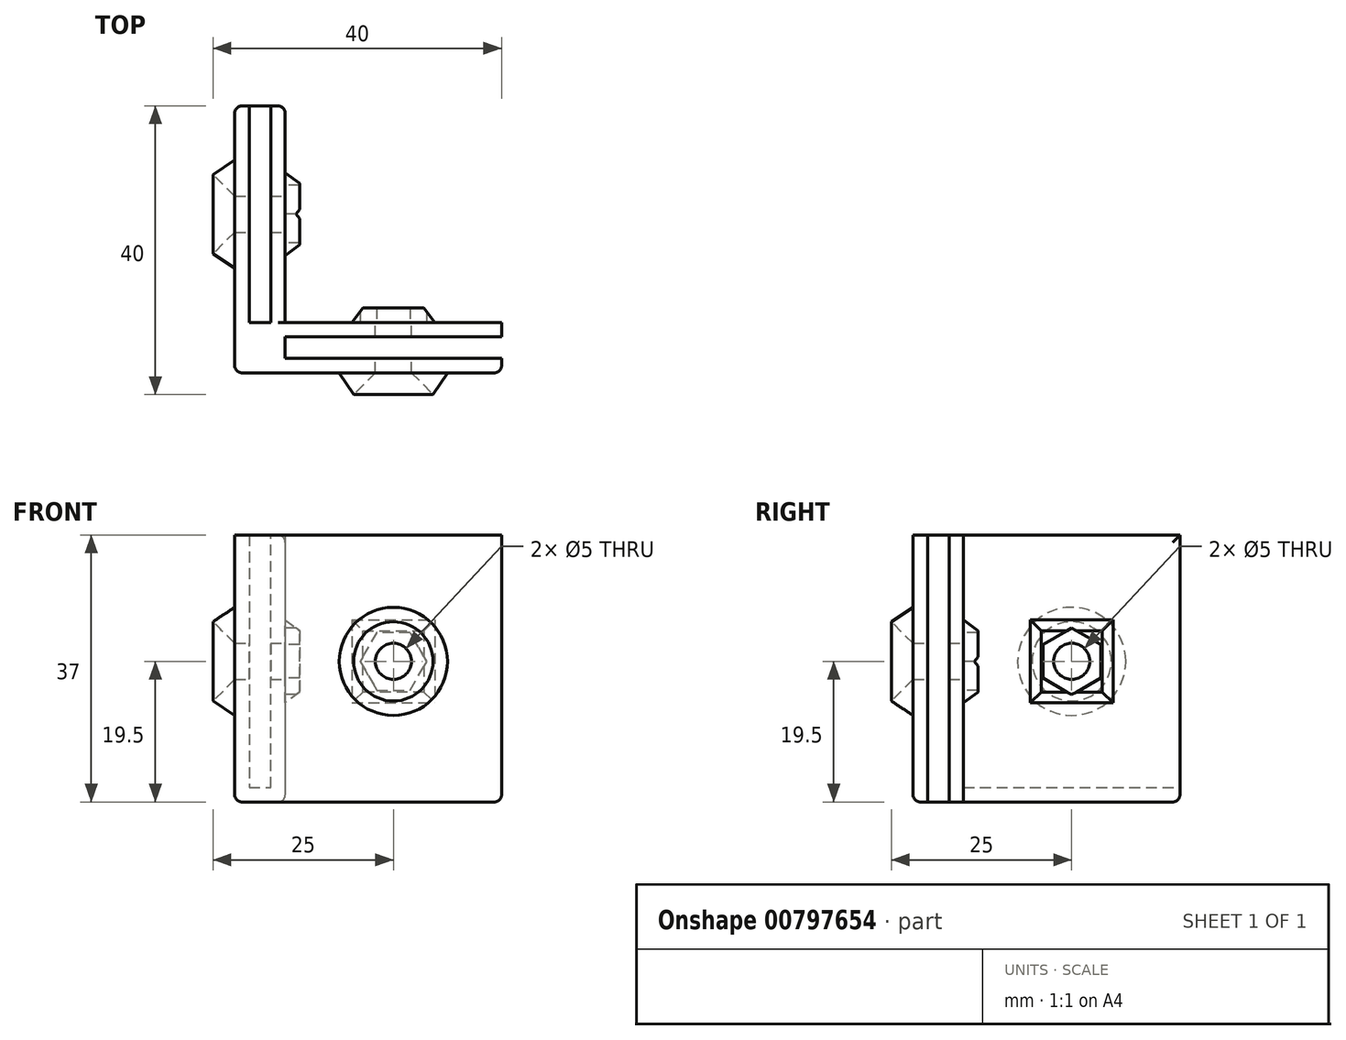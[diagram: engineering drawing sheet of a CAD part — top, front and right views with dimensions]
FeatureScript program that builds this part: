
annotation { "Feature Type Name" : "Feature", "Feature Type Description" : "" }
export const myFeature = defineFeature(function(context is Context, id is Id, definition is map)
    precondition{}
    {
        {
            var Q0;
            Q0=qCreatedBy(makeId("Front.planeOp"),FACE);
            var sketch = newSketch(context, id + "F0", { "sketchPlane" : qUnion([Q0])});
            skLineSegment(sketch, "E0.bottom", {"start": v(18.5, -18.5) * mm, "end": v(-18.5, -18.5) * mm});
            skLineSegment(sketch, "E0.top", {"start": v(18.5, 18.5) * mm, "end": v(-18.5, 18.5) * mm});
            skLineSegment(sketch, "E0.left", {"start": v(18.5, -18.5) * mm, "end": v(18.5, 18.5) * mm});
            skLineSegment(sketch, "E0.right", {"start": v(-18.5, -18.5) * mm, "end": v(-18.5, 18.5) * mm});
            skPoint(sketch, "E0.middle", {"position": v(0, 0) * mm});
            skLineSegment(sketch, "E1", {"start": v(-18.5, 18.5) * mm, "end": v(-16.5, 18.5) * mm});
            skLineSegment(sketch, "E2", {"start": v(-16.5, 18.5) * mm, "end": v(-16.5, -16.5) * mm});
            skLineSegment(sketch, "E3", {"start": v(-16.5, -16.5) * mm, "end": v(-13.5, -16.5) * mm});
            skLineSegment(sketch, "E4", {"start": v(-13.5, -16.5) * mm, "end": v(-13.5, 18.5) * mm});
            skLineSegment(sketch, "E5", {"start": v(-13.5, 18.5) * mm, "end": v(-11.5, 18.5) * mm});
            skLineSegment(sketch, "E6", {"start": v(-11.5, 18.5) * mm, "end": v(-11.5, -18.5) * mm});
            skSolve(sketch);
        }
        {
            var Q0;
            Q0 = qSketchRegion(id + "F0", true);
            extrude(context, id + "F1", {"entities" : qUnion([Q0]), "depth" : 32 * mm, "offsetDistance" : 25 * mm});
        }
        {
            var Q0;
            {var subQ0=sQuery(id+"F0.wireOp",EDGE,"E0.left");Q0=makeQuery(id+"F0.imprint","IMPRINT",FACE,{"disambiguationData":[TD([[makeQuery(id+"F0.imprint","IMPRINT",EDGE,{"derivedFrom":subQ0}),1.0]])]});}
            var Q1;
            {var subQ0=sQuery(id+"F0.wireOp",EDGE,"E2");Q1=makeQuery(id+"F0.imprint","IMPRINT",FACE,{"disambiguationData":[TD([[makeQuery(id+"F0.imprint","IMPRINT",EDGE,{"derivedFrom":subQ0}),1.0]])]});}
            extrude(context, id + "F2", {"entities" : qUnion([Q0, Q1]), "operationType" : NewBodyOperationType.REMOVE, "depth" : 25 * mm, "offsetDistance" : 25 * mm});
        }
        {
            var Q0;
            Q0=makeQuery(id+"F1.opExtrude","SWEPT_FACE",FACE,{"disambiguationData":[OSD([sQuery(id+"F0.wireOp",EDGE,"E0.left")])]});
            var sketch = newSketch(context, id + "F3", { "sketchPlane" : qUnion([Q0])});
            skLineSegment(sketch, "E7", {"start": v(-32, 18.5) * mm, "end": v(-30, 18.5) * mm});
            skLineSegment(sketch, "E8", {"start": v(-30, 18.5) * mm, "end": v(-30, -18.5) * mm});
            skLineSegment(sketch, "E9", {"start": v(-30, -18.5) * mm, "end": v(-27, -18.5) * mm});
            skLineSegment(sketch, "E10", {"start": v(-27, -18.5) * mm, "end": v(-27, 18.5) * mm});
            skLineSegment(sketch, "E11", {"start": v(-27, 18.5) * mm, "end": v(-25, 18.5) * mm});
            skLineSegment(sketch, "E12", {"start": v(-30, -18.5) * mm, "end": v(-30, -16.5) * mm});
            skLineSegment(sketch, "E13", {"start": v(-30, -16.5) * mm, "end": v(-27, -16.5) * mm});
            skSolve(sketch);
        }
        {
            var Q0;
            {var subQ0=sQuery(id+"F3.wireOp",EDGE,"E8");Q0=makeQuery(id+"F3.imprint","IMPRINT",FACE,{"disambiguationData":[TD([[makeQuery(id+"F3.imprint","IMPRINT",EDGE,{"derivedFrom":subQ0}),1.0]])]});}
            extrude(context, id + "F4", {"entities" : qUnion([Q0]), "operationType" : NewBodyOperationType.REMOVE, "oppositeDirection" : true, "depth" : 30 * mm, "offsetDistance" : 25 * mm});
        }
        {
            var Q0;
            Q0=makeQuery(id+"F2.boolean.opBoolean","COPY",FACE,{"derivedFrom":makeQuery(id+"F2.opExtrude","CAP_FACE",FACE,{"disambiguationData":[OSD([sQuery(id+"F0.wireOp",EDGE,"E0.bottom"),sQuery(id+"F0.wireOp",EDGE,"E0.top"),sQuery(id+"F0.wireOp",EDGE,"E0.left"),sQuery(id+"F0.wireOp",EDGE,"E6")])],"isStart":false})});
            var sketch = newSketch(context, id + "F5", { "sketchPlane" : qUnion([Q0])});
            skCircle(sketch, "E14", {"center": v(-3.5, 1) * mm, "radius": 2.5 * mm});
            skCircle(sketch, "E15.cCircle", {"center": v(-3.5, 1) * mm, "radius": 4 * mm, "construction": true});
            skLineSegment(sketch, "E15.0", {"start": v(-5.8, 5) * mm, "end": v(-1.2, 5) * mm});
            skLineSegment(sketch, "E15.1", {"start": v(-1.2, 5) * mm, "end": v(1.12, 1) * mm});
            skLineSegment(sketch, "E15.2", {"start": v(1.12, 1) * mm, "end": v(-1.2, -3) * mm});
            skLineSegment(sketch, "E15.3", {"start": v(-1.2, -3) * mm, "end": v(-5.8, -3) * mm});
            skLineSegment(sketch, "E15.4", {"start": v(-5.8, -3) * mm, "end": v(-8.12, 1) * mm});
            skLineSegment(sketch, "E15.5", {"start": v(-8.12, 1) * mm, "end": v(-5.8, 5) * mm});
            skPoint(sketch, "E15.0.midPoint", {"position": v(-3.5, 5) * mm});
            skLineSegment(sketch, "E16.bottom", {"start": v(2.25, 6.75) * mm, "end": v(-9.25, 6.75) * mm});
            skLineSegment(sketch, "E16.top", {"start": v(2.25, -4.75) * mm, "end": v(-9.25, -4.75) * mm});
            skLineSegment(sketch, "E16.left", {"start": v(2.25, 6.75) * mm, "end": v(2.25, -4.75) * mm});
            skLineSegment(sketch, "E16.right", {"start": v(-9.25, 6.75) * mm, "end": v(-9.25, -4.75) * mm});
            skSolve(sketch);
        }
        {
            var Q0;
            {var subQ3=sQuery(id+"F5.wireOp",EDGE,"E15.1");Q0=makeQuery(id+"F5.imprint","IMPRINT",FACE,{"disambiguationData":[TD([[makeQuery(id+"F5.imprint","IMPRINT",EDGE,{"derivedFrom":subQ3}),1.0]])]});}
            extrude(context, id + "F6", {"entities" : qUnion([Q0]), "operationType" : NewBodyOperationType.ADD, "depth" : 2 * mm, "offsetDistance" : 25 * mm});
        }
        {
            var Q0;
            Q0=makeQuery(id+"F5.imprint","IMPRINT",FACE,{"disambiguationData":[TD([[makeQuery(id+"F5.imprint","IMPRINT",EDGE,{"derivedFrom":sQuery(id+"F5.wireOp",EDGE,"E14")}),1.0]])]});
            extrude(context, id + "F7", {"entities" : qUnion([Q0]), "operationType" : NewBodyOperationType.REMOVE, "oppositeDirection" : true, "depth" : 25 * mm, "offsetDistance" : 25 * mm});
        }
        {
            var Q0;
            Q0=makeQuery(id+"F6.opExtrude","CAP_EDGE",EDGE,{"disambiguationData":[OSD([sQuery(id+"F5.wireOp",EDGE,"E16.right")])],"isStart":false});
            var Q1;
            Q1=makeQuery(id+"F6.opExtrude","CAP_EDGE",EDGE,{"disambiguationData":[OSD([sQuery(id+"F5.wireOp",EDGE,"E16.bottom")])],"isStart":false});
            var Q2;
            Q2=makeQuery(id+"F6.opExtrude","CAP_EDGE",EDGE,{"disambiguationData":[OSD([sQuery(id+"F5.wireOp",EDGE,"E16.left")])],"isStart":false});
            var Q3;
            Q3=makeQuery(id+"F6.opExtrude","CAP_EDGE",EDGE,{"disambiguationData":[OSD([sQuery(id+"F5.wireOp",EDGE,"E16.top")])],"isStart":false});
            chamfer(context, id + "F8", {"entities" : qUnion([Q0, Q1, Q2, Q3]), "chamferType" : ChamferType.TWO_OFFSETS, "width1" : 1.5 * mm, "oppositeDirection" : false, "width2" : 2 * mm, "tangentPropagation" : true});
        }
        {
            var Q0;
            Q0=makeQuery(id+"F1.opExtrude","CAP_FACE",FACE,{"disambiguationData":[OSD([sQuery(id+"F0.wireOp",EDGE,"E0.bottom"),sQuery(id+"F0.wireOp",EDGE,"E0.top"),sQuery(id+"F0.wireOp",EDGE,"E0.left"),sQuery(id+"F0.wireOp",EDGE,"E0.right"),sQuery(id+"F0.wireOp",EDGE,"E1"),sQuery(id+"F0.wireOp",EDGE,"E5")])],"isStart":false});
            var sketch = newSketch(context, id + "F9", { "sketchPlane" : qUnion([Q0])});
            skCircle(sketch, "E17", {"center": v(3.5, 1) * mm, "radius": 7.5 * mm});
            skSolve(sketch);
        }
        {
            var Q0;
            Q0=makeQuery(id+"F9.imprint","IMPRINT",FACE,{"disambiguationData":[TD([[makeQuery(id+"F9.imprint","IMPRINT",EDGE,{"derivedFrom":sQuery(id+"F9.wireOp",EDGE,"E17")}),1.0]])]});
            extrude(context, id + "F10", {"entities" : qUnion([Q0]), "operationType" : NewBodyOperationType.ADD, "depth" : 3 * mm, "offsetDistance" : 25 * mm});
        }
        {
            var Q0;
            Q0=makeQuery(id+"F10.opExtrude","CAP_EDGE",EDGE,{"disambiguationData":[OSD([sQuery(id+"F0.wireOp",EDGE,"E0.bottom"),sQuery(id+"F0.wireOp",EDGE,"E0.top"),sQuery(id+"F0.wireOp",EDGE,"E0.left"),sQuery(id+"F0.wireOp",EDGE,"E0.right"),sQuery(id+"F0.wireOp",EDGE,"E1"),sQuery(id+"F0.wireOp",EDGE,"E5"),sQuery(id+"F5.wireOp",EDGE,"E14")])],"isStart":false});
            chamfer(context, id + "F11", {"entities" : qUnion([Q0]), "width" : 3 * mm, "tangentPropagation" : true});
        }
        {
            var Q0;
            Q0=makeQuery(id+"F2.boolean.opBoolean","COPY",FACE,{"derivedFrom":makeQuery(id+"F2.opExtrude","SWEPT_FACE",FACE,{"disambiguationData":[OSD([sQuery(id+"F0.wireOp",EDGE,"E6")])]})});
            var sketch = newSketch(context, id + "F12", { "sketchPlane" : qUnion([Q0])});
            skCircle(sketch, "E18.cCircle", {"center": v(-10, 1) * mm, "radius": 4 * mm, "construction": true});
            skLineSegment(sketch, "E18.0", {"start": v(-6, 3.3) * mm, "end": v(-6, -1.3) * mm});
            skLineSegment(sketch, "E18.1", {"start": v(-6, -1.3) * mm, "end": v(-10, -3.62) * mm});
            skLineSegment(sketch, "E18.2", {"start": v(-10, -3.62) * mm, "end": v(-14, -1.3) * mm});
            skLineSegment(sketch, "E18.3", {"start": v(-14, -1.3) * mm, "end": v(-14, 3.3) * mm});
            skLineSegment(sketch, "E18.4", {"start": v(-14, 3.3) * mm, "end": v(-10, 5.62) * mm});
            skLineSegment(sketch, "E18.5", {"start": v(-10, 5.62) * mm, "end": v(-6, 3.3) * mm});
            skPoint(sketch, "E18.0.midPoint", {"position": v(-6, 1) * mm});
            skLineSegment(sketch, "E19.bottom", {"start": v(-4.25, -4.75) * mm, "end": v(-15.75, -4.75) * mm});
            skLineSegment(sketch, "E19.top", {"start": v(-4.25, 6.75) * mm, "end": v(-15.75, 6.75) * mm});
            skLineSegment(sketch, "E19.left", {"start": v(-4.25, -4.75) * mm, "end": v(-4.25, 6.75) * mm});
            skLineSegment(sketch, "E19.right", {"start": v(-15.75, -4.75) * mm, "end": v(-15.75, 6.75) * mm});
            skCircle(sketch, "E20", {"center": v(-10, 1) * mm, "radius": 2.5 * mm});
            skSolve(sketch);
        }
        {
            var Q0;
            Q0=makeQuery(id+"F12.imprint","IMPRINT",FACE,{"disambiguationData":[TD([[makeQuery(id+"F12.imprint","IMPRINT",EDGE,{"derivedFrom":sQuery(id+"F12.wireOp",EDGE,"E18.0")}),1.0]])]});
            extrude(context, id + "F13", {"entities" : qUnion([Q0]), "operationType" : NewBodyOperationType.ADD, "depth" : 2 * mm, "offsetDistance" : 25 * mm});
        }
        {
            var Q0;
            Q0=makeQuery(id+"F13.opExtrude","CAP_EDGE",EDGE,{"disambiguationData":[OSD([sQuery(id+"F12.wireOp",EDGE,"E19.left")])],"isStart":false});
            var Q1;
            Q1=makeQuery(id+"F13.opExtrude","CAP_EDGE",EDGE,{"disambiguationData":[OSD([sQuery(id+"F12.wireOp",EDGE,"E19.bottom")])],"isStart":false});
            var Q2;
            Q2=makeQuery(id+"F13.opExtrude","CAP_EDGE",EDGE,{"disambiguationData":[OSD([sQuery(id+"F12.wireOp",EDGE,"E19.right")])],"isStart":false});
            var Q3;
            Q3=makeQuery(id+"F13.opExtrude","CAP_EDGE",EDGE,{"disambiguationData":[OSD([sQuery(id+"F12.wireOp",EDGE,"E19.top")])],"isStart":false});
            chamfer(context, id + "F14", {"entities" : qUnion([Q0, Q1, Q2, Q3]), "chamferType" : ChamferType.TWO_OFFSETS, "width1" : 1.5 * mm, "oppositeDirection" : false, "width2" : 2 * mm, "tangentPropagation" : true});
        }
        {
            var Q0;
            Q0=makeQuery(id+"F12.imprint","IMPRINT",FACE,{"disambiguationData":[TD([[makeQuery(id+"F12.imprint","IMPRINT",EDGE,{"derivedFrom":sQuery(id+"F12.wireOp",EDGE,"E20")}),1.0]])]});
            extrude(context, id + "F15", {"entities" : qUnion([Q0]), "operationType" : NewBodyOperationType.REMOVE, "oppositeDirection" : true, "depth" : 25 * mm, "offsetDistance" : 25 * mm});
        }
        {
            var Q0;
            Q0=makeQuery(id+"F1.opExtrude","SWEPT_FACE",FACE,{"disambiguationData":[OSD([sQuery(id+"F0.wireOp",EDGE,"E0.right")])]});
            var sketch = newSketch(context, id + "F16", { "sketchPlane" : qUnion([Q0])});
            skCircle(sketch, "E21", {"center": v(10, 1) * mm, "radius": 7.5 * mm});
            skSolve(sketch);
        }
        {
            var Q0;
            Q0=makeQuery(id+"F16.imprint","IMPRINT",FACE,{"disambiguationData":[TD([[makeQuery(id+"F16.imprint","IMPRINT",EDGE,{"derivedFrom":sQuery(id+"F16.wireOp",EDGE,"E21")}),1.0]])]});
            extrude(context, id + "F17", {"entities" : qUnion([Q0]), "operationType" : NewBodyOperationType.ADD, "depth" : 3 * mm, "offsetDistance" : 25 * mm});
        }
        {
            var Q0;
            Q0=makeQuery(id+"F17.opExtrude","CAP_EDGE",EDGE,{"disambiguationData":[OSD([sQuery(id+"F0.wireOp",EDGE,"E0.right"),sQuery(id+"F12.wireOp",EDGE,"E20")])],"isStart":false});
            chamfer(context, id + "F18", {"entities" : qUnion([Q0]), "width" : 3 * mm, "tangentPropagation" : true});
        }
        {
            var Q0;
            Q0=makeQuery(id+"F17.opExtrude","CAP_EDGE",EDGE,{"disambiguationData":[OSD([sQuery(id+"F16.wireOp",EDGE,"E21")])],"isStart":false});
            var Q1;
            Q1=makeQuery(id+"F10.opExtrude","CAP_EDGE",EDGE,{"disambiguationData":[OSD([sQuery(id+"F9.wireOp",EDGE,"E17")])],"isStart":false});
            chamfer(context, id + "F19", {"entities" : qUnion([Q0, Q1]), "chamferType" : ChamferType.TWO_OFFSETS, "width1" : 2 * mm, "oppositeDirection" : false, "width2" : 3 * mm, "tangentPropagation" : true});
        }
        {
            var Q0;
            Q0=makeQuery(id+"F1.opExtrude","CAP_FACE",FACE,{"disambiguationData":[OSD([sQuery(id+"F0.wireOp",EDGE,"E0.bottom"),sQuery(id+"F0.wireOp",EDGE,"E0.top"),sQuery(id+"F0.wireOp",EDGE,"E0.left"),sQuery(id+"F0.wireOp",EDGE,"E0.right"),sQuery(id+"F0.wireOp",EDGE,"E1"),sQuery(id+"F0.wireOp",EDGE,"E5")])],"isStart":true});
            var sketch = newSketch(context, id + "F20", { "sketchPlane" : qUnion([Q0])});
            skSolve(sketch);
        }
        {
            var Q0;
            {var subQ2=sQuery(id+"F0.wireOp",EDGE,"E0.right");Q0=makeQuery(id+"F20.imprint","IMPRINT",FACE,{"disambiguationData":[TD([[makeQuery(id+"F20.imprint","IMPRINT",EDGE,{"derivedFrom":makeQuery(id+"F1.opExtrude","CAP_EDGE",EDGE,{"disambiguationData":[OSD([subQ2])],"isStart":true})}),1.0]])]});}
            extrude(context, id + "F21", {"entities" : qUnion([Q0]), "operationType" : NewBodyOperationType.ADD, "depth" : 5 * mm, "offsetDistance" : 25 * mm});
        }
        {
            var Q0;
            Q0=makeQuery(id+"F21.opExtrude","CAP_EDGE",EDGE,{"disambiguationData":[OSD([sQuery(id+"F0.wireOp",EDGE,"E6")])],"isStart":false});
            var Q1;
            Q1=makeQuery(id+"F21.opExtrude","CAP_EDGE",EDGE,{"disambiguationData":[OSD([sQuery(id+"F0.wireOp",EDGE,"E0.right")])],"isStart":false});
            var Q2;
            {var subQ0=sQuery(id+"F0.wireOp",EDGE,"E6");var subQ1=sQuery(id+"F0.wireOp",EDGE,"E0.bottom");Q2=makeQuery(id+"F21.boolean.opBoolean","MERGE",EDGE,{"derivedFrom":[makeQuery(id+"F2.boolean.opBoolean","COPY",EDGE,{"derivedFrom":makeQuery(id+"F2.opExtrude","SWEPT_EDGE",EDGE,{"disambiguationData":[OSD([subQ1,subQ0])]})}),makeQuery(id+"F21.opExtrude","SWEPT_EDGE",EDGE,{"disambiguationData":[OSD([subQ1,subQ0])]})]});}
            var Q3;
            Q3=makeQuery(id+"F2.boolean.opBoolean","COPY",EDGE,{"derivedFrom":makeQuery(id+"F2.opExtrude","CAP_EDGE",EDGE,{"disambiguationData":[OSD([sQuery(id+"F0.wireOp",EDGE,"E0.bottom")])],"isStart":false})});
            var Q4;
            Q4=makeQuery(id+"F1.opExtrude","CAP_EDGE",EDGE,{"disambiguationData":[OSD([sQuery(id+"F0.wireOp",EDGE,"E0.bottom")])],"isStart":false});
            var Q5;
            Q5=makeQuery(id+"F1.opExtrude","CAP_EDGE",EDGE,{"disambiguationData":[OSD([sQuery(id+"F0.wireOp",EDGE,"E0.left")])],"isStart":false});
            var Q6;
            Q6=makeQuery(id+"F2.boolean.opBoolean","COPY",EDGE,{"derivedFrom":makeQuery(id+"F2.opExtrude","CAP_EDGE",EDGE,{"disambiguationData":[OSD([sQuery(id+"F0.wireOp",EDGE,"E0.left")])],"isStart":false})});
            var Q7;
            Q7=makeQuery(id+"F21.opExtrude","CAP_EDGE",EDGE,{"disambiguationData":[OSD([sQuery(id+"F0.wireOp",EDGE,"E0.bottom")])],"isStart":false});
            var Q8;
            {var subQ0=sQuery(id+"F0.wireOp",EDGE,"E0.right");var subQ1=sQuery(id+"F0.wireOp",EDGE,"E0.bottom");Q8=makeQuery(id+"F21.boolean.opBoolean","MERGE",EDGE,{"derivedFrom":[makeQuery(id+"F1.opExtrude","SWEPT_EDGE",EDGE,{"disambiguationData":[OSD([subQ1,subQ0])]}),makeQuery(id+"F21.opExtrude","SWEPT_EDGE",EDGE,{"disambiguationData":[OSD([subQ1,subQ0])]})]});}
            var Q9;
            Q9=makeQuery(id+"F1.opExtrude","SWEPT_EDGE",EDGE,{"disambiguationData":[OSD([sQuery(id+"F0.wireOp",EDGE,"E0.bottom"),sQuery(id+"F0.wireOp",EDGE,"E0.left")])]});
            var Q10;
            Q10=makeQuery(id+"F1.opExtrude","CAP_EDGE",EDGE,{"disambiguationData":[OSD([sQuery(id+"F0.wireOp",EDGE,"E0.right")])],"isStart":false});
            fillet(context, id + "F22", {"entities" : qUnion([Q0, Q1, Q2, Q3, Q4, Q5, Q6, Q7, Q8, Q9, Q10]), "radius" : 1 * mm, "tangentPropagation" : true, "allowEdgeOverflow" : false});
        }
    });
